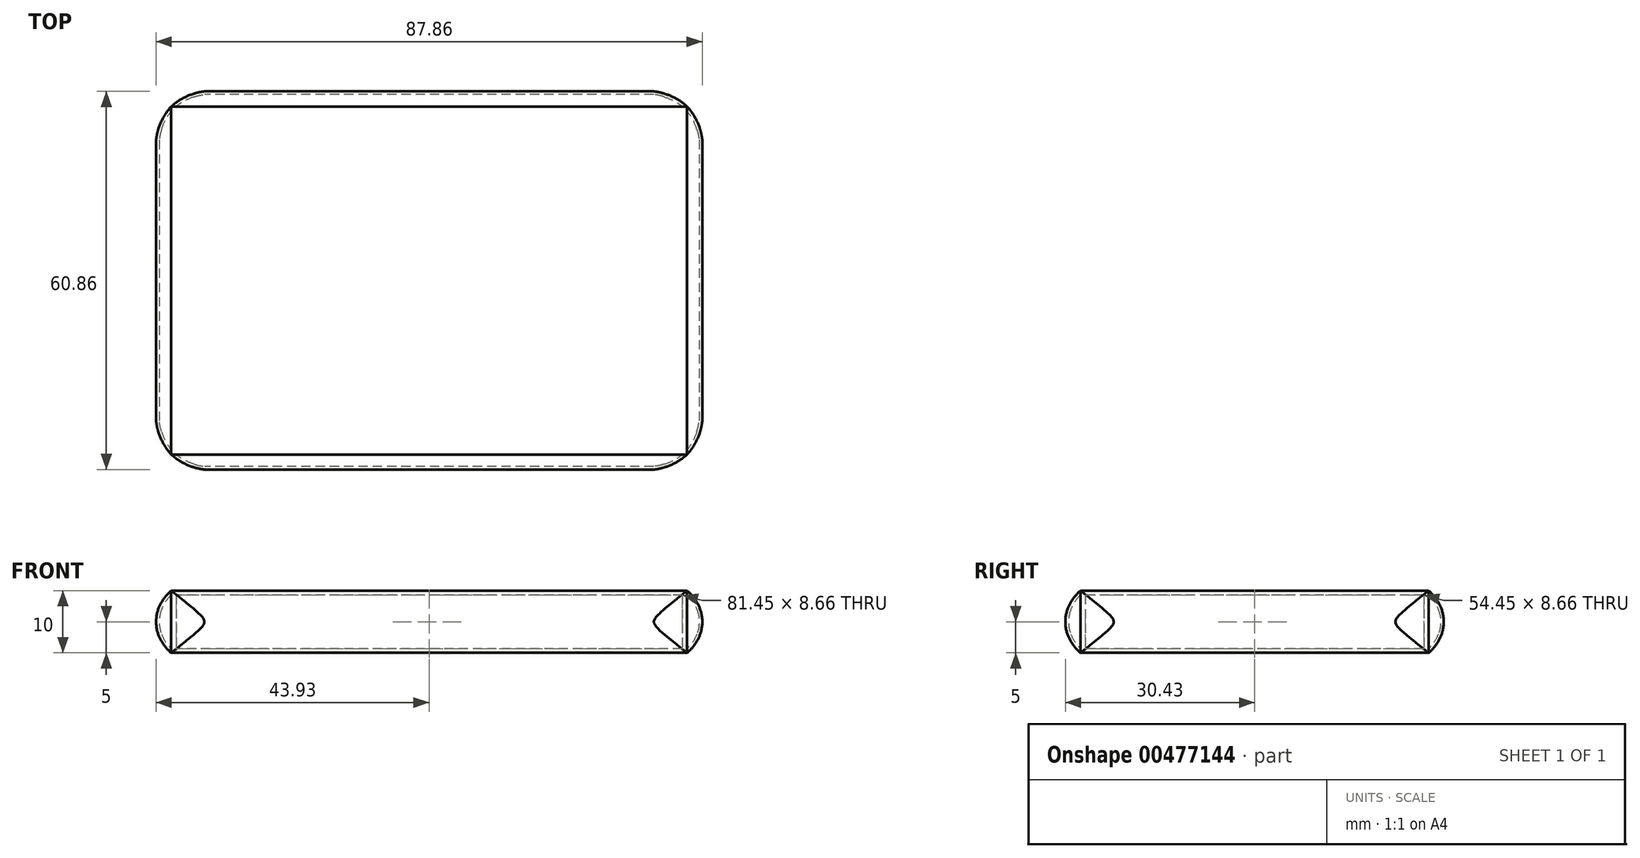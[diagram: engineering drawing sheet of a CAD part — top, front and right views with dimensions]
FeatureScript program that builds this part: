
annotation { "Feature Type Name" : "Feature", "Feature Type Description" : "" }
export const myFeature = defineFeature(function(context is Context, id is Id, definition is map)
    precondition{}
    {
        {
            var Q0;
            Q0=qCreatedBy(makeId("Right.planeOp"),FACE);
            cPlane(context, id + "F0", {"entities" : qUnion([Q0]), "cplaneType" : CPlaneType.OFFSET, "offset" : 41.5 * mm, "width" : 150 * mm, "height" : 150 * mm});
        }
        {
            var Q0;
            Q0=qCreatedBy(makeId("Right.planeOp"),FACE);
            cPlane(context, id + "F1", {"entities" : qUnion([Q0]), "cplaneType" : CPlaneType.OFFSET, "offset" : 29.1 * mm, "width" : 150 * mm, "height" : 150 * mm});
        }
        {
            var Q0;
            Q0=qCreatedBy(makeId("Right.planeOp"),FACE);
            cPlane(context, id + "F2", {"entities" : qUnion([Q0]), "cplaneType" : CPlaneType.OFFSET, "offset" : 25.7 * mm, "oppositeDirection" : true, "width" : 150 * mm, "height" : 150 * mm});
        }
        {
            var Q0;
            Q0=qCreatedBy(makeId("Front.planeOp"),FACE);
            var sketch = newSketch(context, id + "F3", { "sketchPlane" : qUnion([Q0])});
            skLineSegment(sketch, "E0.bottom", {"start": v(41.5, 5) * mm, "end": v(-41.5, 5) * mm});
            skLineSegment(sketch, "E0.top", {"start": v(41.5, -5) * mm, "end": v(-41.5, -5) * mm});
            skLineSegment(sketch, "E0.left", {"start": v(41.5, 5) * mm, "end": v(41.5, -5) * mm});
            skLineSegment(sketch, "E0.right", {"start": v(-41.5, 5) * mm, "end": v(-41.5, -5) * mm});
            skPoint(sketch, "E0.middle", {"position": v(0, 0) * mm});
            skSolve(sketch);
        }
        {
            var Q0;
            Q0=qCreatedBy(id+"F0.planeOp",FACE);
            var sketch = newSketch(context, id + "F4", { "sketchPlane" : qUnion([Q0])});
            skLineSegment(sketch, "E1.bottom", {"start": v(56, 5) * mm, "end": v(0, 5) * mm});
            skLineSegment(sketch, "E1.top", {"start": v(56, -5) * mm, "end": v(0, -5) * mm});
            skLineSegment(sketch, "E1.left", {"start": v(56, 5) * mm, "end": v(56, -5) * mm});
            skLineSegment(sketch, "E1.right", {"start": v(0, 5) * mm, "end": v(0, -5) * mm});
            skPoint(sketch, "E1.middle", {"position": v(28, 0) * mm});
            skSolve(sketch);
        }
        {
            var Q0;
            Q0=makeQuery(id+"F3.imprint","IMPRINT",FACE,{"disambiguationData":[TD([[makeQuery(id+"F3.imprint","IMPRINT",EDGE,{"derivedFrom":sQuery(id+"F3.wireOp",EDGE,"E0.bottom")}),1.0]])]});
            extrude(context, id + "F5", {"entities" : qUnion([Q0]), "depth" : 2.5 * mm});
        }
        {
            var Q0;
            Q0=makeQuery(id+"F4.imprint","IMPRINT",FACE,{"disambiguationData":[TD([[makeQuery(id+"F4.imprint","IMPRINT",EDGE,{"derivedFrom":sQuery(id+"F4.wireOp",EDGE,"E1.bottom")}),1.0]])]});
            extrude(context, id + "F6", {"entities" : qUnion([Q0]), "depth" : 2.5 * mm});
        }
        {
            var Q0;
            Q0=makeQuery(id+"F5.opExtrude","CAP_EDGE",EDGE,{"disambiguationData":[OSD([sQuery(id+"F3.wireOp",EDGE,"E0.right")])],"isStart":false});
            var Q1;
            Q1=makeQuery(id+"F5.opExtrude","CAP_EDGE",EDGE,{"disambiguationData":[OSD([sQuery(id+"F3.wireOp",EDGE,"E0.left")])],"isStart":false});
            var Q2;
            Q2=makeQuery(id+"F6.opExtrude","CAP_EDGE",EDGE,{"disambiguationData":[OSD([sQuery(id+"F4.wireOp",EDGE,"E1.right")])],"isStart":false});
            var Q3;
            Q3=makeQuery(id+"F6.opExtrude","CAP_EDGE",EDGE,{"disambiguationData":[OSD([sQuery(id+"F4.wireOp",EDGE,"E1.left")])],"isStart":false});
            fillet(context, id + "F7", {"entities" : qUnion([Q0, Q1, Q2, Q3]), "radius" : 9.7 * mm, "tangentPropagation" : true, "allowEdgeOverflow" : false});
        }
        {
            var Q0;
            Q0=makeQuery(id+"F5.opExtrude","CAP_EDGE",EDGE,{"disambiguationData":[OSD([sQuery(id+"F3.wireOp",EDGE,"E0.bottom")])],"isStart":false});
            var Q1;
            Q1=makeQuery(id+"F5.opExtrude","CAP_EDGE",EDGE,{"disambiguationData":[OSD([sQuery(id+"F3.wireOp",EDGE,"E0.top")])],"isStart":false});
            var Q2;
            Q2=makeQuery(id+"F6.opExtrude","CAP_EDGE",EDGE,{"disambiguationData":[OSD([sQuery(id+"F4.wireOp",EDGE,"E1.bottom")])],"isStart":false});
            var Q3;
            Q3=makeQuery(id+"F6.opExtrude","CAP_EDGE",EDGE,{"disambiguationData":[OSD([sQuery(id+"F4.wireOp",EDGE,"E1.top")])],"isStart":false});
            fillet(context, id + "F8", {"entities" : qUnion([Q0, Q1, Q2, Q3]), "radius" : 7 * mm, "allowEdgeOverflow" : false});
        }
        {
            var Q0;
            Q0=makeQuery(id+"F8.opFillet","BLEND_EDGE",EDGE,{"blendedFrom":[makeQuery(id+"F5.opExtrude","CAP_EDGE",EDGE,{"disambiguationData":[OSD([sQuery(id+"F3.wireOp",EDGE,"E0.bottom")])],"isStart":false}),makeQuery(id+"F5.opExtrude","CAP_EDGE",EDGE,{"disambiguationData":[OSD([sQuery(id+"F3.wireOp",EDGE,"E0.top")])],"isStart":false})],"blendedInto":[]});
            var Q1;
            Q1=makeQuery(id+"F8.opFillet","BLEND_EDGE",EDGE,{"blendedFrom":[makeQuery(id+"F6.opExtrude","CAP_EDGE",EDGE,{"disambiguationData":[OSD([sQuery(id+"F4.wireOp",EDGE,"E1.bottom")])],"isStart":false}),makeQuery(id+"F6.opExtrude","CAP_EDGE",EDGE,{"disambiguationData":[OSD([sQuery(id+"F4.wireOp",EDGE,"E1.top")])],"isStart":false})],"blendedInto":[]});
            fillet(context, id + "F9", {"entities" : qUnion([Q0, Q1]), "radius" : 6 * mm, "tangentPropagation" : true, "allowEdgeOverflow" : false});
        }
        {
            var Q0;
            Q0=makeQuery(id+"F5.opExtrude","CAP_FACE",FACE,{"disambiguationData":[OSD([sQuery(id+"F3.wireOp",EDGE,"E0.bottom"),sQuery(id+"F3.wireOp",EDGE,"E0.top"),sQuery(id+"F3.wireOp",EDGE,"E0.left"),sQuery(id+"F3.wireOp",EDGE,"E0.right")])],"isStart":true});
            var Q1;
            Q1=makeQuery(id+"F6.opExtrude","CAP_FACE",FACE,{"disambiguationData":[OSD([sQuery(id+"F4.wireOp",EDGE,"E1.bottom"),sQuery(id+"F4.wireOp",EDGE,"E1.top"),sQuery(id+"F4.wireOp",EDGE,"E1.left"),sQuery(id+"F4.wireOp",EDGE,"E1.right")])],"isStart":true});
            shell(context, id + "F10", {"entities" : qUnion([Q0, Q1]), "thickness" : 0.5 * mm});
        }
        {
            var Q0;
            Q0=makeQuery(id+"F6.opExtrude","SWEPT_BODY",BODY,{"disambiguationData":[OSD([sQuery(id+"F4.wireOp",EDGE,"E1.bottom"),sQuery(id+"F4.wireOp",EDGE,"E1.top"),sQuery(id+"F4.wireOp",EDGE,"E1.left"),sQuery(id+"F4.wireOp",EDGE,"E1.right")])]});
            var Q1;
            Q1=qCreatedBy(makeId("Right.planeOp"),FACE);
            mirror(context, id + "F11", {"entities" : qUnion([Q0]), "mirrorPlane" : qUnion([Q1])});
        }
        {
            var Q0;
            Q0=makeQuery(id+"F5.opExtrude","SWEPT_BODY",BODY,{"disambiguationData":[OSD([sQuery(id+"F3.wireOp",EDGE,"E0.bottom"),sQuery(id+"F3.wireOp",EDGE,"E0.top"),sQuery(id+"F3.wireOp",EDGE,"E0.left"),sQuery(id+"F3.wireOp",EDGE,"E0.right")])]});
            var Q1;
            Q1=qCreatedBy(makeId("Front.planeOp"),FACE);
            mirror(context, id + "F12", {"entities" : qUnion([Q0]), "mirrorPlane" : qUnion([Q1])});
        }
        {
            var Q0;
            Q0=makeQuery(id+"F12.opPattern","COPY",BODY,{"derivedFrom":makeQuery(id+"F5.opExtrude","SWEPT_BODY",BODY,{"disambiguationData":[OSD([sQuery(id+"F3.wireOp",EDGE,"E0.bottom"),sQuery(id+"F3.wireOp",EDGE,"E0.top"),sQuery(id+"F3.wireOp",EDGE,"E0.left"),sQuery(id+"F3.wireOp",EDGE,"E0.right")])]}),"instanceName":"1"});
            transform(context, id + "F13", {"entities" : qUnion([Q0]), "transformType" : TransformType.TRANSLATION_3D, "dx" : 0 * mm, "dy" : 56 * mm, "dz" : 0 * mm, "makeCopy" : false});
        }
        {
            var Q0;
            Q0=qCreatedBy(makeId("Front.planeOp"),FACE);
            var sketch = newSketch(context, id + "F14", { "sketchPlane" : qUnion([Q0])});
            skLineSegment(sketch, "E2.0", {"start": v(41.5, -5) * mm, "end": v(-41.5, -5) * mm});
            skPoint(sketch, "E3", {"position": v(0, -5) * mm});
            skPoint(sketch, "E4", {"position": v(-20.4, -5) * mm});
            skPoint(sketch, "E5", {"position": v(23.4, -5) * mm});
            skSolve(sketch);
        }
        {
            var Q0;
            Q0=makeQuery(id+"F12.opPattern","COPY",FACE,{"derivedFrom":makeQuery(id+"F5.opExtrude","CAP_FACE",FACE,{"disambiguationData":[OSD([sQuery(id+"F3.wireOp",EDGE,"E0.bottom"),sQuery(id+"F3.wireOp",EDGE,"E0.top"),sQuery(id+"F3.wireOp",EDGE,"E0.left"),sQuery(id+"F3.wireOp",EDGE,"E0.right")])],"isStart":true}),"instanceName":"1"});
            var sketch = newSketch(context, id + "F15", { "sketchPlane" : qUnion([Q0])});
            skLineSegment(sketch, "E6.0", {"start": v(41.5, -5) * mm, "end": v(-41.5, -5) * mm});
            skPoint(sketch, "E7", {"position": v(0, -5) * mm});
            skPoint(sketch, "E8", {"position": v(-20.4, -5) * mm});
            skPoint(sketch, "E9", {"position": v(23.4, -5) * mm});
            skSolve(sketch);
        }
        {
            var Q0;
            Q0=qCreatedBy(makeId("Right.planeOp"),FACE);
            var sketch = newSketch(context, id + "F16", { "sketchPlane" : qUnion([Q0])});
            skFitSpline(sketch, "E10", {"points": [v(56, -5) * mm, v(0, -5) * mm], "startDerivative": vector(1.85, -1.96) * mm, "endDerivative": vector(1.6, 2.67) * mm});
            skSolve(sketch);
        }
        {
            var Q0;
            Q0=qCreatedBy(id+"F1.planeOp",FACE);
            var sketch = newSketch(context, id + "F17", { "sketchPlane" : qUnion([Q0])});
            skFitSpline(sketch, "E11", {"points": [v(56, -5) * mm, v(0, -5) * mm], "startDerivative": vector(2.26, -10.97) * mm, "endDerivative": vector(0.56, 13.1) * mm});
            skSolve(sketch);
        }
        {
            var Q0;
            Q0=qCreatedBy(id+"F2.planeOp",FACE);
            var sketch = newSketch(context, id + "F18", { "sketchPlane" : qUnion([Q0])});
            skFitSpline(sketch, "E12", {"points": [v(56, -5) * mm, v(0, -5) * mm], "startDerivative": vector(3.76, -8.87) * mm, "endDerivative": vector(0.42, 9.45) * mm});
            skSolve(sketch);
        }
        {
            var Q0;
            Q0=sQuery(id+"F14.wireOp",EDGE,"E2.0");
            var Q1;
            Q1=sQuery(id+"F15.wireOp",EDGE,"E6.0");
            var Q2;
            Q2=sQuery(id+"F16.wireOp",EDGE,"E10");
            var Q3;
            Q3=sQuery(id+"F17.wireOp",EDGE,"E11");
            var Q4;
            Q4=sQuery(id+"F18.wireOp",EDGE,"E12");
            loft(context, id + "F19", {"bodyType" : ToolBodyType.SURFACE, "addGuides" : true, "wireProfilesArray" : [{ "wireProfileEntities" : qUnion([Q0]) }, { "wireProfileEntities" : qUnion([Q1]) }], "guidesArray" : [{ "guideEntities" : qUnion([Q2]), "guideDerivativeType" : LoftGuideDerivativeType.DEFAULT, "guideDerivativeMagnitude" : 1 }, { "guideEntities" : qUnion([Q3]), "guideDerivativeType" : LoftGuideDerivativeType.DEFAULT, "guideDerivativeMagnitude" : 1 }, { "guideEntities" : qUnion([Q4]), "guideDerivativeType" : LoftGuideDerivativeType.DEFAULT, "guideDerivativeMagnitude" : 1 }]});
        }
        {
            var Q0;
            Q0=makeQuery(id+"F19.opLoft","SWEPT_BODY",BODY,{"disambiguationData":[OSD([sQuery(id+"F14.wireOp",EDGE,"E2.0"),sQuery(id+"F15.wireOp",EDGE,"E6.0"),sQuery(id+"F16.wireOp",EDGE,"E10"),sQuery(id+"F17.wireOp",EDGE,"E11"),sQuery(id+"F18.wireOp",EDGE,"E12")])]});
            var Q1;
            Q1=qCreatedBy(makeId("Top.planeOp"),FACE);
            mirror(context, id + "F20", {"entities" : qUnion([Q0]), "mirrorPlane" : qUnion([Q1])});
        }
    });
